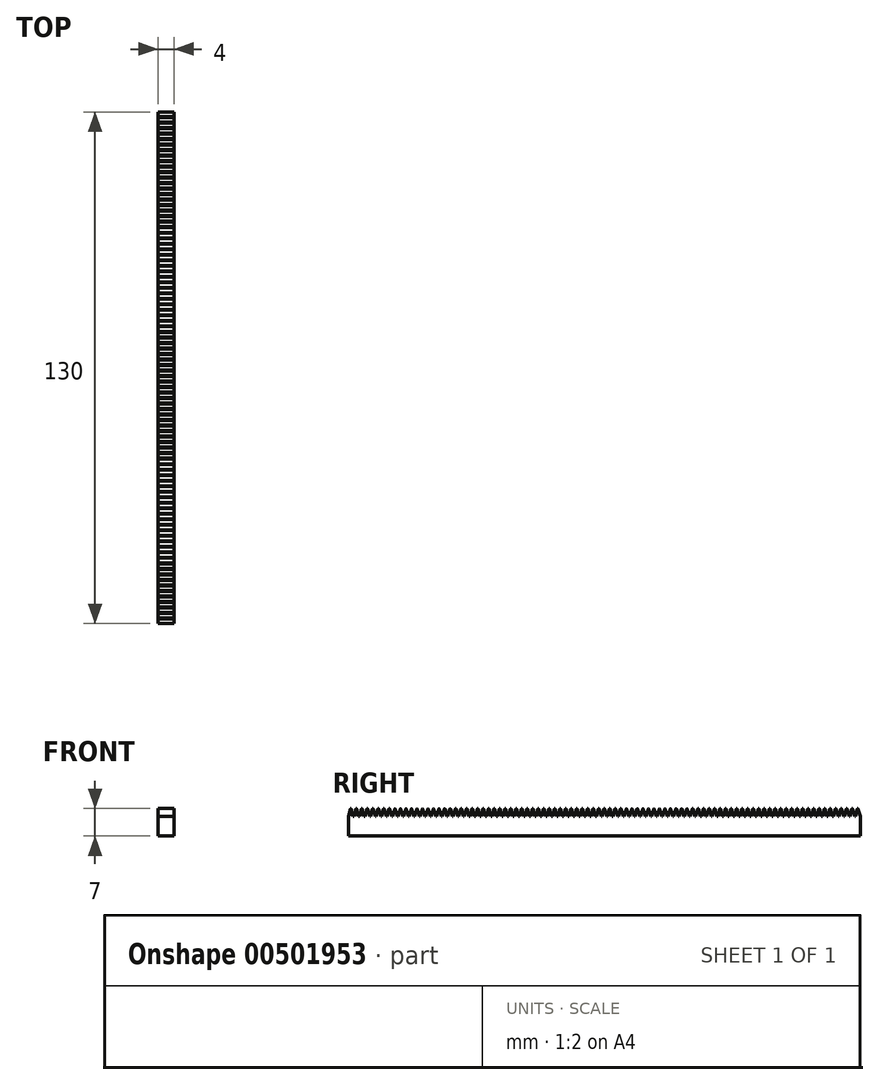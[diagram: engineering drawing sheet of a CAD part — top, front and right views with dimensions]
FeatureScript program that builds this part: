
annotation { "Feature Type Name" : "Feature", "Feature Type Description" : "" }
export const myFeature = defineFeature(function(context is Context, id is Id, definition is map)
    precondition{}
    {
        {
            var Q0;
            Q0=qCreatedBy(makeId("Top.planeOp"),FACE);
            var sketch = newSketch(context, id + "F0", { "sketchPlane" : qUnion([Q0])});
            skLineSegment(sketch, "E0.bottom", {"start": v(2, -65) * mm, "end": v(-2, -65) * mm});
            skLineSegment(sketch, "E0.top", {"start": v(2, 65) * mm, "end": v(-2, 65) * mm});
            skLineSegment(sketch, "E0.left", {"start": v(2, -65) * mm, "end": v(2, 65) * mm});
            skLineSegment(sketch, "E0.right", {"start": v(-2, -65) * mm, "end": v(-2, 65) * mm});
            skPoint(sketch, "E0.middle", {"position": v(0, 0) * mm});
            skSolve(sketch);
        }
        {
            var Q0;
            Q0 = qSketchRegion(id + "F0", true);
            extrude(context, id + "F1", {"entities" : qUnion([Q0]), "depth" : 5 * mm});
        }
        {
            var Q0;
            Q0=makeQuery(id+"F1.opExtrude","SWEPT_FACE",FACE,{"disambiguationData":[OSD([sQuery(id+"F0.wireOp",EDGE,"E0.left")])]});
            var sketch = newSketch(context, id + "F2", { "sketchPlane" : qUnion([Q0])});
            skLineSegment(sketch, "E1", {"start": v(-65, 5) * mm, "end": v(-64.45, 6.96) * mm});
            skLineSegment(sketch, "E2", {"start": v(-64.35, 6.96) * mm, "end": v(-63.8, 5) * mm});
            skLineSegment(sketch, "E3", {"start": v(-63.8, 5) * mm, "end": v(-65, 5) * mm});
            skArc(sketch, "E4.filletArc", {"start": v(-64.35, 6.96) * mm, "mid": v(-64.4, 7) * mm, "end": v(-64.45, 6.96) * mm});
            skPoint(sketch, "E5", {"position": v(-64.4, 7) * mm});
            skLineSegment(sketch, "E6.1.0.0", {"start": v(-63.6, 5) * mm, "end": v(-63.05, 6.96) * mm});
            skLineSegment(sketch, "E6.1.0.1", {"start": v(-62.4, 5) * mm, "end": v(-63.6, 5) * mm});
            skLineSegment(sketch, "E6.1.0.2", {"start": v(-62.95, 6.96) * mm, "end": v(-62.4, 5) * mm});
            skArc(sketch, "E6.1.0.3", {"start": v(-62.95, 6.96) * mm, "mid": v(-63, 7) * mm, "end": v(-63.05, 6.96) * mm});
            skLineSegment(sketch, "E6.2.0.0", {"start": v(-62.2, 5) * mm, "end": v(-61.65, 6.96) * mm});
            skLineSegment(sketch, "E6.2.0.1", {"start": v(-61, 5) * mm, "end": v(-62.2, 5) * mm});
            skLineSegment(sketch, "E6.2.0.2", {"start": v(-61.55, 6.96) * mm, "end": v(-61, 5) * mm});
            skArc(sketch, "E6.2.0.3", {"start": v(-61.55, 6.96) * mm, "mid": v(-61.6, 7) * mm, "end": v(-61.65, 6.96) * mm});
            skLineSegment(sketch, "E6.3.0.0", {"start": v(-60.8, 5) * mm, "end": v(-60.25, 6.96) * mm});
            skLineSegment(sketch, "E6.3.0.1", {"start": v(-59.6, 5) * mm, "end": v(-60.8, 5) * mm});
            skLineSegment(sketch, "E6.3.0.2", {"start": v(-60.15, 6.96) * mm, "end": v(-59.6, 5) * mm});
            skArc(sketch, "E6.3.0.3", {"start": v(-60.15, 6.96) * mm, "mid": v(-60.2, 7) * mm, "end": v(-60.25, 6.96) * mm});
            skLineSegment(sketch, "E6.4.0.0", {"start": v(-59.4, 5) * mm, "end": v(-58.85, 6.96) * mm});
            skLineSegment(sketch, "E6.4.0.1", {"start": v(-58.2, 5) * mm, "end": v(-59.4, 5) * mm});
            skLineSegment(sketch, "E6.4.0.2", {"start": v(-58.75, 6.96) * mm, "end": v(-58.2, 5) * mm});
            skArc(sketch, "E6.4.0.3", {"start": v(-58.75, 6.96) * mm, "mid": v(-58.8, 7) * mm, "end": v(-58.85, 6.96) * mm});
            skLineSegment(sketch, "E6.5.0.0", {"start": v(-58, 5) * mm, "end": v(-57.45, 6.96) * mm});
            skLineSegment(sketch, "E6.5.0.1", {"start": v(-56.8, 5) * mm, "end": v(-58, 5) * mm});
            skLineSegment(sketch, "E6.5.0.2", {"start": v(-57.35, 6.96) * mm, "end": v(-56.8, 5) * mm});
            skArc(sketch, "E6.5.0.3", {"start": v(-57.35, 6.96) * mm, "mid": v(-57.4, 7) * mm, "end": v(-57.45, 6.96) * mm});
            skLineSegment(sketch, "E6.6.0.0", {"start": v(-56.6, 5) * mm, "end": v(-56.05, 6.96) * mm});
            skLineSegment(sketch, "E6.6.0.1", {"start": v(-55.4, 5) * mm, "end": v(-56.6, 5) * mm});
            skLineSegment(sketch, "E6.6.0.2", {"start": v(-55.95, 6.96) * mm, "end": v(-55.4, 5) * mm});
            skArc(sketch, "E6.6.0.3", {"start": v(-55.95, 6.96) * mm, "mid": v(-56, 7) * mm, "end": v(-56.05, 6.96) * mm});
            skLineSegment(sketch, "E6.7.0.0", {"start": v(-55.2, 5) * mm, "end": v(-54.65, 6.96) * mm});
            skLineSegment(sketch, "E6.7.0.1", {"start": v(-54, 5) * mm, "end": v(-55.2, 5) * mm});
            skLineSegment(sketch, "E6.7.0.2", {"start": v(-54.55, 6.96) * mm, "end": v(-54, 5) * mm});
            skArc(sketch, "E6.7.0.3", {"start": v(-54.55, 6.96) * mm, "mid": v(-54.6, 7) * mm, "end": v(-54.65, 6.96) * mm});
            skLineSegment(sketch, "E6.8.0.0", {"start": v(-53.8, 5) * mm, "end": v(-53.25, 6.96) * mm});
            skLineSegment(sketch, "E6.8.0.1", {"start": v(-52.6, 5) * mm, "end": v(-53.8, 5) * mm});
            skLineSegment(sketch, "E6.8.0.2", {"start": v(-53.15, 6.96) * mm, "end": v(-52.6, 5) * mm});
            skArc(sketch, "E6.8.0.3", {"start": v(-53.15, 6.96) * mm, "mid": v(-53.2, 7) * mm, "end": v(-53.25, 6.96) * mm});
            skLineSegment(sketch, "E6.9.0.0", {"start": v(-52.4, 5) * mm, "end": v(-51.85, 6.96) * mm});
            skLineSegment(sketch, "E6.9.0.1", {"start": v(-51.2, 5) * mm, "end": v(-52.4, 5) * mm});
            skLineSegment(sketch, "E6.9.0.2", {"start": v(-51.75, 6.96) * mm, "end": v(-51.2, 5) * mm});
            skArc(sketch, "E6.9.0.3", {"start": v(-51.75, 6.96) * mm, "mid": v(-51.8, 7) * mm, "end": v(-51.85, 6.96) * mm});
            skLineSegment(sketch, "E6.10.0.0", {"start": v(-51, 5) * mm, "end": v(-50.45, 6.96) * mm});
            skLineSegment(sketch, "E6.10.0.1", {"start": v(-49.8, 5) * mm, "end": v(-51, 5) * mm});
            skLineSegment(sketch, "E6.10.0.2", {"start": v(-50.35, 6.96) * mm, "end": v(-49.8, 5) * mm});
            skArc(sketch, "E6.10.0.3", {"start": v(-50.35, 6.96) * mm, "mid": v(-50.4, 7) * mm, "end": v(-50.45, 6.96) * mm});
            skLineSegment(sketch, "E6.11.0.0", {"start": v(-49.6, 5) * mm, "end": v(-49.05, 6.96) * mm});
            skLineSegment(sketch, "E6.11.0.1", {"start": v(-48.4, 5) * mm, "end": v(-49.6, 5) * mm});
            skLineSegment(sketch, "E6.11.0.2", {"start": v(-48.95, 6.96) * mm, "end": v(-48.4, 5) * mm});
            skArc(sketch, "E6.11.0.3", {"start": v(-48.95, 6.96) * mm, "mid": v(-49, 7) * mm, "end": v(-49.05, 6.96) * mm});
            skLineSegment(sketch, "E6.12.0.0", {"start": v(-48.2, 5) * mm, "end": v(-47.65, 6.96) * mm});
            skLineSegment(sketch, "E6.12.0.1", {"start": v(-47, 5) * mm, "end": v(-48.2, 5) * mm});
            skLineSegment(sketch, "E6.12.0.2", {"start": v(-47.55, 6.96) * mm, "end": v(-47, 5) * mm});
            skArc(sketch, "E6.12.0.3", {"start": v(-47.55, 6.96) * mm, "mid": v(-47.6, 7) * mm, "end": v(-47.65, 6.96) * mm});
            skLineSegment(sketch, "E6.13.0.0", {"start": v(-46.8, 5) * mm, "end": v(-46.25, 6.96) * mm});
            skLineSegment(sketch, "E6.13.0.1", {"start": v(-45.6, 5) * mm, "end": v(-46.8, 5) * mm});
            skLineSegment(sketch, "E6.13.0.2", {"start": v(-46.15, 6.96) * mm, "end": v(-45.6, 5) * mm});
            skArc(sketch, "E6.13.0.3", {"start": v(-46.15, 6.96) * mm, "mid": v(-46.2, 7) * mm, "end": v(-46.25, 6.96) * mm});
            skLineSegment(sketch, "E6.14.0.0", {"start": v(-45.4, 5) * mm, "end": v(-44.85, 6.96) * mm});
            skLineSegment(sketch, "E6.14.0.1", {"start": v(-44.2, 5) * mm, "end": v(-45.4, 5) * mm});
            skLineSegment(sketch, "E6.14.0.2", {"start": v(-44.75, 6.96) * mm, "end": v(-44.2, 5) * mm});
            skArc(sketch, "E6.14.0.3", {"start": v(-44.75, 6.96) * mm, "mid": v(-44.8, 7) * mm, "end": v(-44.85, 6.96) * mm});
            skLineSegment(sketch, "E6.15.0.0", {"start": v(-44, 5) * mm, "end": v(-43.45, 6.96) * mm});
            skLineSegment(sketch, "E6.15.0.1", {"start": v(-42.8, 5) * mm, "end": v(-44, 5) * mm});
            skLineSegment(sketch, "E6.15.0.2", {"start": v(-43.35, 6.96) * mm, "end": v(-42.8, 5) * mm});
            skArc(sketch, "E6.15.0.3", {"start": v(-43.35, 6.96) * mm, "mid": v(-43.4, 7) * mm, "end": v(-43.45, 6.96) * mm});
            skLineSegment(sketch, "E6.16.0.0", {"start": v(-42.6, 5) * mm, "end": v(-42.05, 6.96) * mm});
            skLineSegment(sketch, "E6.16.0.1", {"start": v(-41.4, 5) * mm, "end": v(-42.6, 5) * mm});
            skLineSegment(sketch, "E6.16.0.2", {"start": v(-41.95, 6.96) * mm, "end": v(-41.4, 5) * mm});
            skArc(sketch, "E6.16.0.3", {"start": v(-41.95, 6.96) * mm, "mid": v(-42, 7) * mm, "end": v(-42.05, 6.96) * mm});
            skLineSegment(sketch, "E6.17.0.0", {"start": v(-41.2, 5) * mm, "end": v(-40.65, 6.96) * mm});
            skLineSegment(sketch, "E6.17.0.1", {"start": v(-40, 5) * mm, "end": v(-41.2, 5) * mm});
            skLineSegment(sketch, "E6.17.0.2", {"start": v(-40.55, 6.96) * mm, "end": v(-40, 5) * mm});
            skArc(sketch, "E6.17.0.3", {"start": v(-40.55, 6.96) * mm, "mid": v(-40.6, 7) * mm, "end": v(-40.65, 6.96) * mm});
            skLineSegment(sketch, "E6.18.0.0", {"start": v(-39.8, 5) * mm, "end": v(-39.25, 6.96) * mm});
            skLineSegment(sketch, "E6.18.0.1", {"start": v(-38.6, 5) * mm, "end": v(-39.8, 5) * mm});
            skLineSegment(sketch, "E6.18.0.2", {"start": v(-39.15, 6.96) * mm, "end": v(-38.6, 5) * mm});
            skArc(sketch, "E6.18.0.3", {"start": v(-39.15, 6.96) * mm, "mid": v(-39.2, 7) * mm, "end": v(-39.25, 6.96) * mm});
            skLineSegment(sketch, "E6.19.0.0", {"start": v(-38.4, 5) * mm, "end": v(-37.85, 6.96) * mm});
            skLineSegment(sketch, "E6.19.0.1", {"start": v(-37.2, 5) * mm, "end": v(-38.4, 5) * mm});
            skLineSegment(sketch, "E6.19.0.2", {"start": v(-37.75, 6.96) * mm, "end": v(-37.2, 5) * mm});
            skArc(sketch, "E6.19.0.3", {"start": v(-37.75, 6.96) * mm, "mid": v(-37.8, 7) * mm, "end": v(-37.85, 6.96) * mm});
            skLineSegment(sketch, "E6.20.0.0", {"start": v(-37, 5) * mm, "end": v(-36.45, 6.96) * mm});
            skLineSegment(sketch, "E6.20.0.1", {"start": v(-35.8, 5) * mm, "end": v(-37, 5) * mm});
            skLineSegment(sketch, "E6.20.0.2", {"start": v(-36.35, 6.96) * mm, "end": v(-35.8, 5) * mm});
            skArc(sketch, "E6.20.0.3", {"start": v(-36.35, 6.96) * mm, "mid": v(-36.4, 7) * mm, "end": v(-36.45, 6.96) * mm});
            skLineSegment(sketch, "E6.21.0.0", {"start": v(-35.6, 5) * mm, "end": v(-35.05, 6.96) * mm});
            skLineSegment(sketch, "E6.21.0.1", {"start": v(-34.4, 5) * mm, "end": v(-35.6, 5) * mm});
            skLineSegment(sketch, "E6.21.0.2", {"start": v(-34.95, 6.96) * mm, "end": v(-34.4, 5) * mm});
            skArc(sketch, "E6.21.0.3", {"start": v(-34.95, 6.96) * mm, "mid": v(-35, 7) * mm, "end": v(-35.05, 6.96) * mm});
            skLineSegment(sketch, "E6.22.0.0", {"start": v(-34.2, 5) * mm, "end": v(-33.65, 6.96) * mm});
            skLineSegment(sketch, "E6.22.0.1", {"start": v(-33, 5) * mm, "end": v(-34.2, 5) * mm});
            skLineSegment(sketch, "E6.22.0.2", {"start": v(-33.55, 6.96) * mm, "end": v(-33, 5) * mm});
            skArc(sketch, "E6.22.0.3", {"start": v(-33.55, 6.96) * mm, "mid": v(-33.6, 7) * mm, "end": v(-33.65, 6.96) * mm});
            skLineSegment(sketch, "E6.23.0.0", {"start": v(-32.8, 5) * mm, "end": v(-32.25, 6.96) * mm});
            skLineSegment(sketch, "E6.23.0.1", {"start": v(-31.6, 5) * mm, "end": v(-32.8, 5) * mm});
            skLineSegment(sketch, "E6.23.0.2", {"start": v(-32.15, 6.96) * mm, "end": v(-31.6, 5) * mm});
            skArc(sketch, "E6.23.0.3", {"start": v(-32.15, 6.96) * mm, "mid": v(-32.2, 7) * mm, "end": v(-32.25, 6.96) * mm});
            skLineSegment(sketch, "E6.24.0.0", {"start": v(-31.4, 5) * mm, "end": v(-30.85, 6.96) * mm});
            skLineSegment(sketch, "E6.24.0.1", {"start": v(-30.2, 5) * mm, "end": v(-31.4, 5) * mm});
            skLineSegment(sketch, "E6.24.0.2", {"start": v(-30.75, 6.96) * mm, "end": v(-30.2, 5) * mm});
            skArc(sketch, "E6.24.0.3", {"start": v(-30.75, 6.96) * mm, "mid": v(-30.8, 7) * mm, "end": v(-30.85, 6.96) * mm});
            skLineSegment(sketch, "E6.25.0.0", {"start": v(-30, 5) * mm, "end": v(-29.45, 6.96) * mm});
            skLineSegment(sketch, "E6.25.0.1", {"start": v(-28.8, 5) * mm, "end": v(-30, 5) * mm});
            skLineSegment(sketch, "E6.25.0.2", {"start": v(-29.35, 6.96) * mm, "end": v(-28.8, 5) * mm});
            skArc(sketch, "E6.25.0.3", {"start": v(-29.35, 6.96) * mm, "mid": v(-29.4, 7) * mm, "end": v(-29.45, 6.96) * mm});
            skLineSegment(sketch, "E6.26.0.0", {"start": v(-28.6, 5) * mm, "end": v(-28.05, 6.96) * mm});
            skLineSegment(sketch, "E6.26.0.1", {"start": v(-27.4, 5) * mm, "end": v(-28.6, 5) * mm});
            skLineSegment(sketch, "E6.26.0.2", {"start": v(-27.95, 6.96) * mm, "end": v(-27.4, 5) * mm});
            skArc(sketch, "E6.26.0.3", {"start": v(-27.95, 6.96) * mm, "mid": v(-28, 7) * mm, "end": v(-28.05, 6.96) * mm});
            skLineSegment(sketch, "E6.27.0.0", {"start": v(-27.2, 5) * mm, "end": v(-26.65, 6.96) * mm});
            skLineSegment(sketch, "E6.27.0.1", {"start": v(-26, 5) * mm, "end": v(-27.2, 5) * mm});
            skLineSegment(sketch, "E6.27.0.2", {"start": v(-26.55, 6.96) * mm, "end": v(-26, 5) * mm});
            skArc(sketch, "E6.27.0.3", {"start": v(-26.55, 6.96) * mm, "mid": v(-26.6, 7) * mm, "end": v(-26.65, 6.96) * mm});
            skLineSegment(sketch, "E6.28.0.0", {"start": v(-25.8, 5) * mm, "end": v(-25.25, 6.96) * mm});
            skLineSegment(sketch, "E6.28.0.1", {"start": v(-24.6, 5) * mm, "end": v(-25.8, 5) * mm});
            skLineSegment(sketch, "E6.28.0.2", {"start": v(-25.15, 6.96) * mm, "end": v(-24.6, 5) * mm});
            skArc(sketch, "E6.28.0.3", {"start": v(-25.15, 6.96) * mm, "mid": v(-25.2, 7) * mm, "end": v(-25.25, 6.96) * mm});
            skLineSegment(sketch, "E6.29.0.0", {"start": v(-24.4, 5) * mm, "end": v(-23.85, 6.96) * mm});
            skLineSegment(sketch, "E6.29.0.1", {"start": v(-23.2, 5) * mm, "end": v(-24.4, 5) * mm});
            skLineSegment(sketch, "E6.29.0.2", {"start": v(-23.75, 6.96) * mm, "end": v(-23.2, 5) * mm});
            skArc(sketch, "E6.29.0.3", {"start": v(-23.75, 6.96) * mm, "mid": v(-23.8, 7) * mm, "end": v(-23.85, 6.96) * mm});
            skLineSegment(sketch, "E6.30.0.0", {"start": v(-23, 5) * mm, "end": v(-22.45, 6.96) * mm});
            skLineSegment(sketch, "E6.30.0.1", {"start": v(-21.8, 5) * mm, "end": v(-23, 5) * mm});
            skLineSegment(sketch, "E6.30.0.2", {"start": v(-22.35, 6.96) * mm, "end": v(-21.8, 5) * mm});
            skArc(sketch, "E6.30.0.3", {"start": v(-22.35, 6.96) * mm, "mid": v(-22.4, 7) * mm, "end": v(-22.45, 6.96) * mm});
            skLineSegment(sketch, "E6.31.0.0", {"start": v(-21.6, 5) * mm, "end": v(-21.05, 6.96) * mm});
            skLineSegment(sketch, "E6.31.0.1", {"start": v(-20.4, 5) * mm, "end": v(-21.6, 5) * mm});
            skLineSegment(sketch, "E6.31.0.2", {"start": v(-20.95, 6.96) * mm, "end": v(-20.4, 5) * mm});
            skArc(sketch, "E6.31.0.3", {"start": v(-20.95, 6.96) * mm, "mid": v(-21, 7) * mm, "end": v(-21.05, 6.96) * mm});
            skLineSegment(sketch, "E6.32.0.0", {"start": v(-20.2, 5) * mm, "end": v(-19.65, 6.96) * mm});
            skLineSegment(sketch, "E6.32.0.1", {"start": v(-19, 5) * mm, "end": v(-20.2, 5) * mm});
            skLineSegment(sketch, "E6.32.0.2", {"start": v(-19.55, 6.96) * mm, "end": v(-19, 5) * mm});
            skArc(sketch, "E6.32.0.3", {"start": v(-19.55, 6.96) * mm, "mid": v(-19.6, 7) * mm, "end": v(-19.65, 6.96) * mm});
            skLineSegment(sketch, "E6.33.0.0", {"start": v(-18.8, 5) * mm, "end": v(-18.25, 6.96) * mm});
            skLineSegment(sketch, "E6.33.0.1", {"start": v(-17.6, 5) * mm, "end": v(-18.8, 5) * mm});
            skLineSegment(sketch, "E6.33.0.2", {"start": v(-18.15, 6.96) * mm, "end": v(-17.6, 5) * mm});
            skArc(sketch, "E6.33.0.3", {"start": v(-18.15, 6.96) * mm, "mid": v(-18.2, 7) * mm, "end": v(-18.25, 6.96) * mm});
            skLineSegment(sketch, "E6.34.0.0", {"start": v(-17.4, 5) * mm, "end": v(-16.85, 6.96) * mm});
            skLineSegment(sketch, "E6.34.0.1", {"start": v(-16.2, 5) * mm, "end": v(-17.4, 5) * mm});
            skLineSegment(sketch, "E6.34.0.2", {"start": v(-16.75, 6.96) * mm, "end": v(-16.2, 5) * mm});
            skArc(sketch, "E6.34.0.3", {"start": v(-16.75, 6.96) * mm, "mid": v(-16.8, 7) * mm, "end": v(-16.85, 6.96) * mm});
            skLineSegment(sketch, "E6.35.0.0", {"start": v(-16, 5) * mm, "end": v(-15.45, 6.96) * mm});
            skLineSegment(sketch, "E6.35.0.1", {"start": v(-14.8, 5) * mm, "end": v(-16, 5) * mm});
            skLineSegment(sketch, "E6.35.0.2", {"start": v(-15.35, 6.96) * mm, "end": v(-14.8, 5) * mm});
            skArc(sketch, "E6.35.0.3", {"start": v(-15.35, 6.96) * mm, "mid": v(-15.4, 7) * mm, "end": v(-15.45, 6.96) * mm});
            skLineSegment(sketch, "E6.36.0.0", {"start": v(-14.6, 5) * mm, "end": v(-14.05, 6.96) * mm});
            skLineSegment(sketch, "E6.36.0.1", {"start": v(-13.4, 5) * mm, "end": v(-14.6, 5) * mm});
            skLineSegment(sketch, "E6.36.0.2", {"start": v(-13.95, 6.96) * mm, "end": v(-13.4, 5) * mm});
            skArc(sketch, "E6.36.0.3", {"start": v(-13.95, 6.96) * mm, "mid": v(-14, 7) * mm, "end": v(-14.05, 6.96) * mm});
            skLineSegment(sketch, "E6.37.0.0", {"start": v(-13.2, 5) * mm, "end": v(-12.65, 6.96) * mm});
            skLineSegment(sketch, "E6.37.0.1", {"start": v(-12, 5) * mm, "end": v(-13.2, 5) * mm});
            skLineSegment(sketch, "E6.37.0.2", {"start": v(-12.55, 6.96) * mm, "end": v(-12, 5) * mm});
            skArc(sketch, "E6.37.0.3", {"start": v(-12.55, 6.96) * mm, "mid": v(-12.6, 7) * mm, "end": v(-12.65, 6.96) * mm});
            skLineSegment(sketch, "E6.38.0.0", {"start": v(-11.8, 5) * mm, "end": v(-11.25, 6.96) * mm});
            skLineSegment(sketch, "E6.38.0.1", {"start": v(-10.6, 5) * mm, "end": v(-11.8, 5) * mm});
            skLineSegment(sketch, "E6.38.0.2", {"start": v(-11.15, 6.96) * mm, "end": v(-10.6, 5) * mm});
            skArc(sketch, "E6.38.0.3", {"start": v(-11.15, 6.96) * mm, "mid": v(-11.2, 7) * mm, "end": v(-11.25, 6.96) * mm});
            skLineSegment(sketch, "E6.39.0.0", {"start": v(-10.4, 5) * mm, "end": v(-9.85, 6.96) * mm});
            skLineSegment(sketch, "E6.39.0.1", {"start": v(-9.2, 5) * mm, "end": v(-10.4, 5) * mm});
            skLineSegment(sketch, "E6.39.0.2", {"start": v(-9.75, 6.96) * mm, "end": v(-9.2, 5) * mm});
            skArc(sketch, "E6.39.0.3", {"start": v(-9.75, 6.96) * mm, "mid": v(-9.8, 7) * mm, "end": v(-9.85, 6.96) * mm});
            skLineSegment(sketch, "E6.40.0.0", {"start": v(-9, 5) * mm, "end": v(-8.45, 6.96) * mm});
            skLineSegment(sketch, "E6.40.0.1", {"start": v(-7.8, 5) * mm, "end": v(-9, 5) * mm});
            skLineSegment(sketch, "E6.40.0.2", {"start": v(-8.35, 6.96) * mm, "end": v(-7.8, 5) * mm});
            skArc(sketch, "E6.40.0.3", {"start": v(-8.35, 6.96) * mm, "mid": v(-8.4, 7) * mm, "end": v(-8.45, 6.96) * mm});
            skLineSegment(sketch, "E6.41.0.0", {"start": v(-7.6, 5) * mm, "end": v(-7.05, 6.96) * mm});
            skLineSegment(sketch, "E6.41.0.1", {"start": v(-6.4, 5) * mm, "end": v(-7.6, 5) * mm});
            skLineSegment(sketch, "E6.41.0.2", {"start": v(-6.95, 6.96) * mm, "end": v(-6.4, 5) * mm});
            skArc(sketch, "E6.41.0.3", {"start": v(-6.95, 6.96) * mm, "mid": v(-7, 7) * mm, "end": v(-7.05, 6.96) * mm});
            skLineSegment(sketch, "E6.42.0.0", {"start": v(-6.2, 5) * mm, "end": v(-5.65, 6.96) * mm});
            skLineSegment(sketch, "E6.42.0.1", {"start": v(-5, 5) * mm, "end": v(-6.2, 5) * mm});
            skLineSegment(sketch, "E6.42.0.2", {"start": v(-5.55, 6.96) * mm, "end": v(-5, 5) * mm});
            skArc(sketch, "E6.42.0.3", {"start": v(-5.55, 6.96) * mm, "mid": v(-5.6, 7) * mm, "end": v(-5.65, 6.96) * mm});
            skLineSegment(sketch, "E6.43.0.0", {"start": v(-4.8, 5) * mm, "end": v(-4.25, 6.96) * mm});
            skLineSegment(sketch, "E6.43.0.1", {"start": v(-3.6, 5) * mm, "end": v(-4.8, 5) * mm});
            skLineSegment(sketch, "E6.43.0.2", {"start": v(-4.15, 6.96) * mm, "end": v(-3.6, 5) * mm});
            skArc(sketch, "E6.43.0.3", {"start": v(-4.15, 6.96) * mm, "mid": v(-4.2, 7) * mm, "end": v(-4.25, 6.96) * mm});
            skLineSegment(sketch, "E6.44.0.0", {"start": v(-3.4, 5) * mm, "end": v(-2.85, 6.96) * mm});
            skLineSegment(sketch, "E6.44.0.1", {"start": v(-2.2, 5) * mm, "end": v(-3.4, 5) * mm});
            skLineSegment(sketch, "E6.44.0.2", {"start": v(-2.75, 6.96) * mm, "end": v(-2.2, 5) * mm});
            skArc(sketch, "E6.44.0.3", {"start": v(-2.75, 6.96) * mm, "mid": v(-2.8, 7) * mm, "end": v(-2.85, 6.96) * mm});
            skLineSegment(sketch, "E6.45.0.0", {"start": v(-2, 5) * mm, "end": v(-1.45, 6.96) * mm});
            skLineSegment(sketch, "E6.45.0.1", {"start": v(-0.8, 5) * mm, "end": v(-2, 5) * mm});
            skLineSegment(sketch, "E6.45.0.2", {"start": v(-1.35, 6.96) * mm, "end": v(-0.8, 5) * mm});
            skArc(sketch, "E6.45.0.3", {"start": v(-1.35, 6.96) * mm, "mid": v(-1.4, 7) * mm, "end": v(-1.45, 6.96) * mm});
            skLineSegment(sketch, "E6.46.0.0", {"start": v(-0.6, 5) * mm, "end": v(-0.05, 6.96) * mm});
            skLineSegment(sketch, "E6.46.0.1", {"start": v(0.6, 5) * mm, "end": v(-0.6, 5) * mm});
            skLineSegment(sketch, "E6.46.0.2", {"start": v(0.05, 6.96) * mm, "end": v(0.6, 5) * mm});
            skArc(sketch, "E6.46.0.3", {"start": v(0.05, 6.96) * mm, "mid": v(0, 7) * mm, "end": v(-0.05, 6.96) * mm});
            skLineSegment(sketch, "E6.47.0.0", {"start": v(0.8, 5) * mm, "end": v(1.35, 6.96) * mm});
            skLineSegment(sketch, "E6.47.0.1", {"start": v(2, 5) * mm, "end": v(0.8, 5) * mm});
            skLineSegment(sketch, "E6.47.0.2", {"start": v(1.45, 6.96) * mm, "end": v(2, 5) * mm});
            skArc(sketch, "E6.47.0.3", {"start": v(1.45, 6.96) * mm, "mid": v(1.4, 7) * mm, "end": v(1.35, 6.96) * mm});
            skLineSegment(sketch, "E6.48.0.0", {"start": v(2.2, 5) * mm, "end": v(2.75, 6.96) * mm});
            skLineSegment(sketch, "E6.48.0.1", {"start": v(3.4, 5) * mm, "end": v(2.2, 5) * mm});
            skLineSegment(sketch, "E6.48.0.2", {"start": v(2.85, 6.96) * mm, "end": v(3.4, 5) * mm});
            skArc(sketch, "E6.48.0.3", {"start": v(2.85, 6.96) * mm, "mid": v(2.8, 7) * mm, "end": v(2.75, 6.96) * mm});
            skLineSegment(sketch, "E6.49.0.0", {"start": v(3.6, 5) * mm, "end": v(4.15, 6.96) * mm});
            skLineSegment(sketch, "E6.49.0.1", {"start": v(4.8, 5) * mm, "end": v(3.6, 5) * mm});
            skLineSegment(sketch, "E6.49.0.2", {"start": v(4.25, 6.96) * mm, "end": v(4.8, 5) * mm});
            skArc(sketch, "E6.49.0.3", {"start": v(4.25, 6.96) * mm, "mid": v(4.2, 7) * mm, "end": v(4.15, 6.96) * mm});
            skLineSegment(sketch, "E6.50.0.0", {"start": v(5, 5) * mm, "end": v(5.55, 6.96) * mm});
            skLineSegment(sketch, "E6.50.0.1", {"start": v(6.2, 5) * mm, "end": v(5, 5) * mm});
            skLineSegment(sketch, "E6.50.0.2", {"start": v(5.65, 6.96) * mm, "end": v(6.2, 5) * mm});
            skArc(sketch, "E6.50.0.3", {"start": v(5.65, 6.96) * mm, "mid": v(5.6, 7) * mm, "end": v(5.55, 6.96) * mm});
            skLineSegment(sketch, "E6.51.0.0", {"start": v(6.4, 5) * mm, "end": v(6.95, 6.96) * mm});
            skLineSegment(sketch, "E6.51.0.1", {"start": v(7.6, 5) * mm, "end": v(6.4, 5) * mm});
            skLineSegment(sketch, "E6.51.0.2", {"start": v(7.05, 6.96) * mm, "end": v(7.6, 5) * mm});
            skArc(sketch, "E6.51.0.3", {"start": v(7.05, 6.96) * mm, "mid": v(7, 7) * mm, "end": v(6.95, 6.96) * mm});
            skLineSegment(sketch, "E6.52.0.0", {"start": v(7.8, 5) * mm, "end": v(8.35, 6.96) * mm});
            skLineSegment(sketch, "E6.52.0.1", {"start": v(9, 5) * mm, "end": v(7.8, 5) * mm});
            skLineSegment(sketch, "E6.52.0.2", {"start": v(8.45, 6.96) * mm, "end": v(9, 5) * mm});
            skArc(sketch, "E6.52.0.3", {"start": v(8.45, 6.96) * mm, "mid": v(8.4, 7) * mm, "end": v(8.35, 6.96) * mm});
            skLineSegment(sketch, "E6.53.0.0", {"start": v(9.2, 5) * mm, "end": v(9.75, 6.96) * mm});
            skLineSegment(sketch, "E6.53.0.1", {"start": v(10.4, 5) * mm, "end": v(9.2, 5) * mm});
            skLineSegment(sketch, "E6.53.0.2", {"start": v(9.85, 6.96) * mm, "end": v(10.4, 5) * mm});
            skArc(sketch, "E6.53.0.3", {"start": v(9.85, 6.96) * mm, "mid": v(9.8, 7) * mm, "end": v(9.75, 6.96) * mm});
            skLineSegment(sketch, "E6.54.0.0", {"start": v(10.6, 5) * mm, "end": v(11.15, 6.96) * mm});
            skLineSegment(sketch, "E6.54.0.1", {"start": v(11.8, 5) * mm, "end": v(10.6, 5) * mm});
            skLineSegment(sketch, "E6.54.0.2", {"start": v(11.25, 6.96) * mm, "end": v(11.8, 5) * mm});
            skArc(sketch, "E6.54.0.3", {"start": v(11.25, 6.96) * mm, "mid": v(11.2, 7) * mm, "end": v(11.15, 6.96) * mm});
            skLineSegment(sketch, "E6.55.0.0", {"start": v(12, 5) * mm, "end": v(12.55, 6.96) * mm});
            skLineSegment(sketch, "E6.55.0.1", {"start": v(13.2, 5) * mm, "end": v(12, 5) * mm});
            skLineSegment(sketch, "E6.55.0.2", {"start": v(12.65, 6.96) * mm, "end": v(13.2, 5) * mm});
            skArc(sketch, "E6.55.0.3", {"start": v(12.65, 6.96) * mm, "mid": v(12.6, 7) * mm, "end": v(12.55, 6.96) * mm});
            skLineSegment(sketch, "E6.56.0.0", {"start": v(13.4, 5) * mm, "end": v(13.95, 6.96) * mm});
            skLineSegment(sketch, "E6.56.0.1", {"start": v(14.6, 5) * mm, "end": v(13.4, 5) * mm});
            skLineSegment(sketch, "E6.56.0.2", {"start": v(14.05, 6.96) * mm, "end": v(14.6, 5) * mm});
            skArc(sketch, "E6.56.0.3", {"start": v(14.05, 6.96) * mm, "mid": v(14, 7) * mm, "end": v(13.95, 6.96) * mm});
            skLineSegment(sketch, "E6.57.0.0", {"start": v(14.8, 5) * mm, "end": v(15.35, 6.96) * mm});
            skLineSegment(sketch, "E6.57.0.1", {"start": v(16, 5) * mm, "end": v(14.8, 5) * mm});
            skLineSegment(sketch, "E6.57.0.2", {"start": v(15.45, 6.96) * mm, "end": v(16, 5) * mm});
            skArc(sketch, "E6.57.0.3", {"start": v(15.45, 6.96) * mm, "mid": v(15.4, 7) * mm, "end": v(15.35, 6.96) * mm});
            skLineSegment(sketch, "E6.58.0.0", {"start": v(16.2, 5) * mm, "end": v(16.75, 6.96) * mm});
            skLineSegment(sketch, "E6.58.0.1", {"start": v(17.4, 5) * mm, "end": v(16.2, 5) * mm});
            skLineSegment(sketch, "E6.58.0.2", {"start": v(16.85, 6.96) * mm, "end": v(17.4, 5) * mm});
            skArc(sketch, "E6.58.0.3", {"start": v(16.85, 6.96) * mm, "mid": v(16.8, 7) * mm, "end": v(16.75, 6.96) * mm});
            skLineSegment(sketch, "E6.59.0.0", {"start": v(17.6, 5) * mm, "end": v(18.15, 6.96) * mm});
            skLineSegment(sketch, "E6.59.0.1", {"start": v(18.8, 5) * mm, "end": v(17.6, 5) * mm});
            skLineSegment(sketch, "E6.59.0.2", {"start": v(18.25, 6.96) * mm, "end": v(18.8, 5) * mm});
            skArc(sketch, "E6.59.0.3", {"start": v(18.25, 6.96) * mm, "mid": v(18.2, 7) * mm, "end": v(18.15, 6.96) * mm});
            skLineSegment(sketch, "E6.60.0.0", {"start": v(19, 5) * mm, "end": v(19.55, 6.96) * mm});
            skLineSegment(sketch, "E6.60.0.1", {"start": v(20.2, 5) * mm, "end": v(19, 5) * mm});
            skLineSegment(sketch, "E6.60.0.2", {"start": v(19.65, 6.96) * mm, "end": v(20.2, 5) * mm});
            skArc(sketch, "E6.60.0.3", {"start": v(19.65, 6.96) * mm, "mid": v(19.6, 7) * mm, "end": v(19.55, 6.96) * mm});
            skLineSegment(sketch, "E6.61.0.0", {"start": v(20.4, 5) * mm, "end": v(20.95, 6.96) * mm});
            skLineSegment(sketch, "E6.61.0.1", {"start": v(21.6, 5) * mm, "end": v(20.4, 5) * mm});
            skLineSegment(sketch, "E6.61.0.2", {"start": v(21.05, 6.96) * mm, "end": v(21.6, 5) * mm});
            skArc(sketch, "E6.61.0.3", {"start": v(21.05, 6.96) * mm, "mid": v(21, 7) * mm, "end": v(20.95, 6.96) * mm});
            skLineSegment(sketch, "E6.62.0.0", {"start": v(21.8, 5) * mm, "end": v(22.35, 6.96) * mm});
            skLineSegment(sketch, "E6.62.0.1", {"start": v(23, 5) * mm, "end": v(21.8, 5) * mm});
            skLineSegment(sketch, "E6.62.0.2", {"start": v(22.45, 6.96) * mm, "end": v(23, 5) * mm});
            skArc(sketch, "E6.62.0.3", {"start": v(22.45, 6.96) * mm, "mid": v(22.4, 7) * mm, "end": v(22.35, 6.96) * mm});
            skLineSegment(sketch, "E6.63.0.0", {"start": v(23.2, 5) * mm, "end": v(23.75, 6.96) * mm});
            skLineSegment(sketch, "E6.63.0.1", {"start": v(24.4, 5) * mm, "end": v(23.2, 5) * mm});
            skLineSegment(sketch, "E6.63.0.2", {"start": v(23.85, 6.96) * mm, "end": v(24.4, 5) * mm});
            skArc(sketch, "E6.63.0.3", {"start": v(23.85, 6.96) * mm, "mid": v(23.8, 7) * mm, "end": v(23.75, 6.96) * mm});
            skLineSegment(sketch, "E6.64.0.0", {"start": v(24.6, 5) * mm, "end": v(25.15, 6.96) * mm});
            skLineSegment(sketch, "E6.64.0.1", {"start": v(25.8, 5) * mm, "end": v(24.6, 5) * mm});
            skLineSegment(sketch, "E6.64.0.2", {"start": v(25.25, 6.96) * mm, "end": v(25.8, 5) * mm});
            skArc(sketch, "E6.64.0.3", {"start": v(25.25, 6.96) * mm, "mid": v(25.2, 7) * mm, "end": v(25.15, 6.96) * mm});
            skLineSegment(sketch, "E6.65.0.0", {"start": v(26, 5) * mm, "end": v(26.55, 6.96) * mm});
            skLineSegment(sketch, "E6.65.0.1", {"start": v(27.2, 5) * mm, "end": v(26, 5) * mm});
            skLineSegment(sketch, "E6.65.0.2", {"start": v(26.65, 6.96) * mm, "end": v(27.2, 5) * mm});
            skArc(sketch, "E6.65.0.3", {"start": v(26.65, 6.96) * mm, "mid": v(26.6, 7) * mm, "end": v(26.55, 6.96) * mm});
            skLineSegment(sketch, "E6.66.0.0", {"start": v(27.4, 5) * mm, "end": v(27.95, 6.96) * mm});
            skLineSegment(sketch, "E6.66.0.1", {"start": v(28.6, 5) * mm, "end": v(27.4, 5) * mm});
            skLineSegment(sketch, "E6.66.0.2", {"start": v(28.05, 6.96) * mm, "end": v(28.6, 5) * mm});
            skArc(sketch, "E6.66.0.3", {"start": v(28.05, 6.96) * mm, "mid": v(28, 7) * mm, "end": v(27.95, 6.96) * mm});
            skLineSegment(sketch, "E6.67.0.0", {"start": v(28.8, 5) * mm, "end": v(29.35, 6.96) * mm});
            skLineSegment(sketch, "E6.67.0.1", {"start": v(30, 5) * mm, "end": v(28.8, 5) * mm});
            skLineSegment(sketch, "E6.67.0.2", {"start": v(29.45, 6.96) * mm, "end": v(30, 5) * mm});
            skArc(sketch, "E6.67.0.3", {"start": v(29.45, 6.96) * mm, "mid": v(29.4, 7) * mm, "end": v(29.35, 6.96) * mm});
            skLineSegment(sketch, "E6.68.0.0", {"start": v(30.2, 5) * mm, "end": v(30.75, 6.96) * mm});
            skLineSegment(sketch, "E6.68.0.1", {"start": v(31.4, 5) * mm, "end": v(30.2, 5) * mm});
            skLineSegment(sketch, "E6.68.0.2", {"start": v(30.85, 6.96) * mm, "end": v(31.4, 5) * mm});
            skArc(sketch, "E6.68.0.3", {"start": v(30.85, 6.96) * mm, "mid": v(30.8, 7) * mm, "end": v(30.75, 6.96) * mm});
            skLineSegment(sketch, "E6.69.0.0", {"start": v(31.6, 5) * mm, "end": v(32.15, 6.96) * mm});
            skLineSegment(sketch, "E6.69.0.1", {"start": v(32.8, 5) * mm, "end": v(31.6, 5) * mm});
            skLineSegment(sketch, "E6.69.0.2", {"start": v(32.25, 6.96) * mm, "end": v(32.8, 5) * mm});
            skArc(sketch, "E6.69.0.3", {"start": v(32.25, 6.96) * mm, "mid": v(32.2, 7) * mm, "end": v(32.15, 6.96) * mm});
            skLineSegment(sketch, "E6.70.0.0", {"start": v(33, 5) * mm, "end": v(33.55, 6.96) * mm});
            skLineSegment(sketch, "E6.70.0.1", {"start": v(34.2, 5) * mm, "end": v(33, 5) * mm});
            skLineSegment(sketch, "E6.70.0.2", {"start": v(33.65, 6.96) * mm, "end": v(34.2, 5) * mm});
            skArc(sketch, "E6.70.0.3", {"start": v(33.65, 6.96) * mm, "mid": v(33.6, 7) * mm, "end": v(33.55, 6.96) * mm});
            skLineSegment(sketch, "E6.71.0.0", {"start": v(34.4, 5) * mm, "end": v(34.95, 6.96) * mm});
            skLineSegment(sketch, "E6.71.0.1", {"start": v(35.6, 5) * mm, "end": v(34.4, 5) * mm});
            skLineSegment(sketch, "E6.71.0.2", {"start": v(35.05, 6.96) * mm, "end": v(35.6, 5) * mm});
            skArc(sketch, "E6.71.0.3", {"start": v(35.05, 6.96) * mm, "mid": v(35, 7) * mm, "end": v(34.95, 6.96) * mm});
            skLineSegment(sketch, "E6.72.0.0", {"start": v(35.8, 5) * mm, "end": v(36.35, 6.96) * mm});
            skLineSegment(sketch, "E6.72.0.1", {"start": v(37, 5) * mm, "end": v(35.8, 5) * mm});
            skLineSegment(sketch, "E6.72.0.2", {"start": v(36.45, 6.96) * mm, "end": v(37, 5) * mm});
            skArc(sketch, "E6.72.0.3", {"start": v(36.45, 6.96) * mm, "mid": v(36.4, 7) * mm, "end": v(36.35, 6.96) * mm});
            skLineSegment(sketch, "E6.73.0.0", {"start": v(37.2, 5) * mm, "end": v(37.75, 6.96) * mm});
            skLineSegment(sketch, "E6.73.0.1", {"start": v(38.4, 5) * mm, "end": v(37.2, 5) * mm});
            skLineSegment(sketch, "E6.73.0.2", {"start": v(37.85, 6.96) * mm, "end": v(38.4, 5) * mm});
            skArc(sketch, "E6.73.0.3", {"start": v(37.85, 6.96) * mm, "mid": v(37.8, 7) * mm, "end": v(37.75, 6.96) * mm});
            skLineSegment(sketch, "E6.74.0.0", {"start": v(38.6, 5) * mm, "end": v(39.15, 6.96) * mm});
            skLineSegment(sketch, "E6.74.0.1", {"start": v(39.8, 5) * mm, "end": v(38.6, 5) * mm});
            skLineSegment(sketch, "E6.74.0.2", {"start": v(39.25, 6.96) * mm, "end": v(39.8, 5) * mm});
            skArc(sketch, "E6.74.0.3", {"start": v(39.25, 6.96) * mm, "mid": v(39.2, 7) * mm, "end": v(39.15, 6.96) * mm});
            skLineSegment(sketch, "E6.75.0.0", {"start": v(40, 5) * mm, "end": v(40.55, 6.96) * mm});
            skLineSegment(sketch, "E6.75.0.1", {"start": v(41.2, 5) * mm, "end": v(40, 5) * mm});
            skLineSegment(sketch, "E6.75.0.2", {"start": v(40.65, 6.96) * mm, "end": v(41.2, 5) * mm});
            skArc(sketch, "E6.75.0.3", {"start": v(40.65, 6.96) * mm, "mid": v(40.6, 7) * mm, "end": v(40.55, 6.96) * mm});
            skLineSegment(sketch, "E6.76.0.0", {"start": v(41.4, 5) * mm, "end": v(41.95, 6.96) * mm});
            skLineSegment(sketch, "E6.76.0.1", {"start": v(42.6, 5) * mm, "end": v(41.4, 5) * mm});
            skLineSegment(sketch, "E6.76.0.2", {"start": v(42.05, 6.96) * mm, "end": v(42.6, 5) * mm});
            skArc(sketch, "E6.76.0.3", {"start": v(42.05, 6.96) * mm, "mid": v(42, 7) * mm, "end": v(41.95, 6.96) * mm});
            skLineSegment(sketch, "E6.77.0.0", {"start": v(42.8, 5) * mm, "end": v(43.35, 6.96) * mm});
            skLineSegment(sketch, "E6.77.0.1", {"start": v(44, 5) * mm, "end": v(42.8, 5) * mm});
            skLineSegment(sketch, "E6.77.0.2", {"start": v(43.45, 6.96) * mm, "end": v(44, 5) * mm});
            skArc(sketch, "E6.77.0.3", {"start": v(43.45, 6.96) * mm, "mid": v(43.4, 7) * mm, "end": v(43.35, 6.96) * mm});
            skLineSegment(sketch, "E6.78.0.0", {"start": v(44.2, 5) * mm, "end": v(44.75, 6.96) * mm});
            skLineSegment(sketch, "E6.78.0.1", {"start": v(45.4, 5) * mm, "end": v(44.2, 5) * mm});
            skLineSegment(sketch, "E6.78.0.2", {"start": v(44.85, 6.96) * mm, "end": v(45.4, 5) * mm});
            skArc(sketch, "E6.78.0.3", {"start": v(44.85, 6.96) * mm, "mid": v(44.8, 7) * mm, "end": v(44.75, 6.96) * mm});
            skLineSegment(sketch, "E6.79.0.0", {"start": v(45.6, 5) * mm, "end": v(46.15, 6.96) * mm});
            skLineSegment(sketch, "E6.79.0.1", {"start": v(46.8, 5) * mm, "end": v(45.6, 5) * mm});
            skLineSegment(sketch, "E6.79.0.2", {"start": v(46.25, 6.96) * mm, "end": v(46.8, 5) * mm});
            skArc(sketch, "E6.79.0.3", {"start": v(46.25, 6.96) * mm, "mid": v(46.2, 7) * mm, "end": v(46.15, 6.96) * mm});
            skLineSegment(sketch, "E6.80.0.0", {"start": v(47, 5) * mm, "end": v(47.55, 6.96) * mm});
            skLineSegment(sketch, "E6.80.0.1", {"start": v(48.2, 5) * mm, "end": v(47, 5) * mm});
            skLineSegment(sketch, "E6.80.0.2", {"start": v(47.65, 6.96) * mm, "end": v(48.2, 5) * mm});
            skArc(sketch, "E6.80.0.3", {"start": v(47.65, 6.96) * mm, "mid": v(47.6, 7) * mm, "end": v(47.55, 6.96) * mm});
            skLineSegment(sketch, "E6.81.0.0", {"start": v(48.4, 5) * mm, "end": v(48.95, 6.96) * mm});
            skLineSegment(sketch, "E6.81.0.1", {"start": v(49.6, 5) * mm, "end": v(48.4, 5) * mm});
            skLineSegment(sketch, "E6.81.0.2", {"start": v(49.05, 6.96) * mm, "end": v(49.6, 5) * mm});
            skArc(sketch, "E6.81.0.3", {"start": v(49.05, 6.96) * mm, "mid": v(49, 7) * mm, "end": v(48.95, 6.96) * mm});
            skLineSegment(sketch, "E6.82.0.0", {"start": v(49.8, 5) * mm, "end": v(50.35, 6.96) * mm});
            skLineSegment(sketch, "E6.82.0.1", {"start": v(51, 5) * mm, "end": v(49.8, 5) * mm});
            skLineSegment(sketch, "E6.82.0.2", {"start": v(50.45, 6.96) * mm, "end": v(51, 5) * mm});
            skArc(sketch, "E6.82.0.3", {"start": v(50.45, 6.96) * mm, "mid": v(50.4, 7) * mm, "end": v(50.35, 6.96) * mm});
            skLineSegment(sketch, "E6.83.0.0", {"start": v(51.2, 5) * mm, "end": v(51.75, 6.96) * mm});
            skLineSegment(sketch, "E6.83.0.1", {"start": v(52.4, 5) * mm, "end": v(51.2, 5) * mm});
            skLineSegment(sketch, "E6.83.0.2", {"start": v(51.85, 6.96) * mm, "end": v(52.4, 5) * mm});
            skArc(sketch, "E6.83.0.3", {"start": v(51.85, 6.96) * mm, "mid": v(51.8, 7) * mm, "end": v(51.75, 6.96) * mm});
            skLineSegment(sketch, "E6.84.0.0", {"start": v(52.6, 5) * mm, "end": v(53.15, 6.96) * mm});
            skLineSegment(sketch, "E6.84.0.1", {"start": v(53.8, 5) * mm, "end": v(52.6, 5) * mm});
            skLineSegment(sketch, "E6.84.0.2", {"start": v(53.25, 6.96) * mm, "end": v(53.8, 5) * mm});
            skArc(sketch, "E6.84.0.3", {"start": v(53.25, 6.96) * mm, "mid": v(53.2, 7) * mm, "end": v(53.15, 6.96) * mm});
            skLineSegment(sketch, "E6.85.0.0", {"start": v(54, 5) * mm, "end": v(54.55, 6.96) * mm});
            skLineSegment(sketch, "E6.85.0.1", {"start": v(55.2, 5) * mm, "end": v(54, 5) * mm});
            skLineSegment(sketch, "E6.85.0.2", {"start": v(54.65, 6.96) * mm, "end": v(55.2, 5) * mm});
            skArc(sketch, "E6.85.0.3", {"start": v(54.65, 6.96) * mm, "mid": v(54.6, 7) * mm, "end": v(54.55, 6.96) * mm});
            skLineSegment(sketch, "E6.86.0.0", {"start": v(55.4, 5) * mm, "end": v(55.95, 6.96) * mm});
            skLineSegment(sketch, "E6.86.0.1", {"start": v(56.6, 5) * mm, "end": v(55.4, 5) * mm});
            skLineSegment(sketch, "E6.86.0.2", {"start": v(56.05, 6.96) * mm, "end": v(56.6, 5) * mm});
            skArc(sketch, "E6.86.0.3", {"start": v(56.05, 6.96) * mm, "mid": v(56, 7) * mm, "end": v(55.95, 6.96) * mm});
            skLineSegment(sketch, "E6.87.0.0", {"start": v(56.8, 5) * mm, "end": v(57.35, 6.96) * mm});
            skLineSegment(sketch, "E6.87.0.1", {"start": v(58, 5) * mm, "end": v(56.8, 5) * mm});
            skLineSegment(sketch, "E6.87.0.2", {"start": v(57.45, 6.96) * mm, "end": v(58, 5) * mm});
            skArc(sketch, "E6.87.0.3", {"start": v(57.45, 6.96) * mm, "mid": v(57.4, 7) * mm, "end": v(57.35, 6.96) * mm});
            skLineSegment(sketch, "E6.88.0.0", {"start": v(58.2, 5) * mm, "end": v(58.75, 6.96) * mm});
            skLineSegment(sketch, "E6.88.0.1", {"start": v(59.4, 5) * mm, "end": v(58.2, 5) * mm});
            skLineSegment(sketch, "E6.88.0.2", {"start": v(58.85, 6.96) * mm, "end": v(59.4, 5) * mm});
            skArc(sketch, "E6.88.0.3", {"start": v(58.85, 6.96) * mm, "mid": v(58.8, 7) * mm, "end": v(58.75, 6.96) * mm});
            skLineSegment(sketch, "E6.89.0.0", {"start": v(59.6, 5) * mm, "end": v(60.15, 6.96) * mm});
            skLineSegment(sketch, "E6.89.0.1", {"start": v(60.8, 5) * mm, "end": v(59.6, 5) * mm});
            skLineSegment(sketch, "E6.89.0.2", {"start": v(60.25, 6.96) * mm, "end": v(60.8, 5) * mm});
            skArc(sketch, "E6.89.0.3", {"start": v(60.25, 6.96) * mm, "mid": v(60.2, 7) * mm, "end": v(60.15, 6.96) * mm});
            skLineSegment(sketch, "E6.90.0.0", {"start": v(61, 5) * mm, "end": v(61.55, 6.96) * mm});
            skLineSegment(sketch, "E6.90.0.1", {"start": v(62.2, 5) * mm, "end": v(61, 5) * mm});
            skLineSegment(sketch, "E6.90.0.2", {"start": v(61.65, 6.96) * mm, "end": v(62.2, 5) * mm});
            skArc(sketch, "E6.90.0.3", {"start": v(61.65, 6.96) * mm, "mid": v(61.6, 7) * mm, "end": v(61.55, 6.96) * mm});
            skLineSegment(sketch, "E6.91.0.0", {"start": v(62.4, 5) * mm, "end": v(62.95, 6.96) * mm});
            skLineSegment(sketch, "E6.91.0.1", {"start": v(63.6, 5) * mm, "end": v(62.4, 5) * mm});
            skLineSegment(sketch, "E6.91.0.2", {"start": v(63.05, 6.96) * mm, "end": v(63.6, 5) * mm});
            skArc(sketch, "E6.91.0.3", {"start": v(63.05, 6.96) * mm, "mid": v(63, 7) * mm, "end": v(62.95, 6.96) * mm});
            skLineSegment(sketch, "E6.92.0.0", {"start": v(63.8, 5) * mm, "end": v(64.35, 6.96) * mm});
            skLineSegment(sketch, "E6.92.0.1", {"start": v(65, 5) * mm, "end": v(63.8, 5) * mm});
            skLineSegment(sketch, "E6.92.0.2", {"start": v(64.45, 6.96) * mm, "end": v(65, 5) * mm});
            skArc(sketch, "E6.92.0.3", {"start": v(64.45, 6.96) * mm, "mid": v(64.4, 7) * mm, "end": v(64.35, 6.96) * mm});
            skLineSegment(sketch, "E6.direction1", {"start": v(-65, 5) * mm, "end": v(-63.6, 5) * mm, "construction": true});
            skPoint(sketch, "E7", {"position": v(-64.4, 5) * mm});
            skPoint(sketch, "E8", {"position": v(-64.4, 5.93) * mm});
            skSolve(sketch);
        }
        {
            var Q0;
            Q0 = qSketchRegion(id + "F2", true);
            extrude(context, id + "F3", {"entities" : qUnion([Q0]), "operationType" : NewBodyOperationType.ADD, "oppositeDirection" : true, "depth" : 4 * mm});
        }
    });
